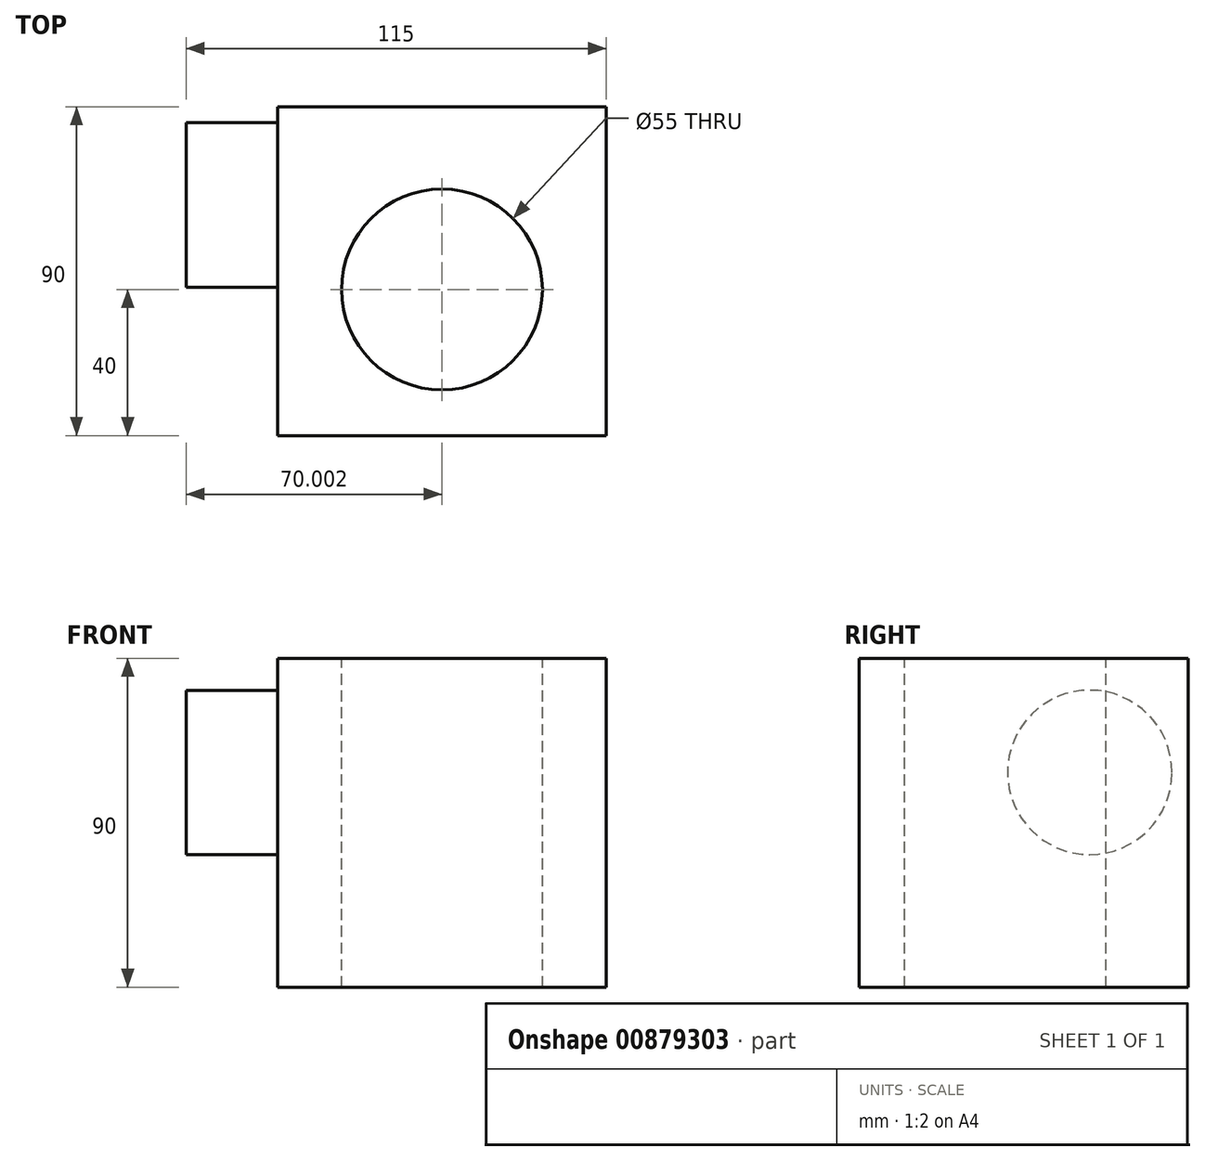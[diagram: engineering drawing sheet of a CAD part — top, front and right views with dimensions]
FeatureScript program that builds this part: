
annotation { "Feature Type Name" : "Feature", "Feature Type Description" : "" }
export const myFeature = defineFeature(function(context is Context, id is Id, definition is map)
    precondition{}
    {
        {
            var Q0;
            Q0=qCreatedBy(makeId("Front.planeOp"),FACE);
            var sketch = newSketch(context, id + "F0", { "sketchPlane" : qUnion([Q0])});
            skLineSegment(sketch, "E0.bottom", {"start": v(-42.19, 55.55) * mm, "end": v(47.81, 55.55) * mm});
            skLineSegment(sketch, "E0.top", {"start": v(-42.19, -34.45) * mm, "end": v(47.81, -34.45) * mm});
            skLineSegment(sketch, "E0.left", {"start": v(-42.19, 55.55) * mm, "end": v(-42.19, -34.45) * mm});
            skLineSegment(sketch, "E0.right", {"start": v(47.81, 55.55) * mm, "end": v(47.81, -34.45) * mm});
            skSolve(sketch);
        }
        {
            var Q0;
            Q0 = qSketchRegion(id + "F0", true);
            extrude(context, id + "F1", {"entities" : qUnion([Q0]), "depth" : 90 * mm, "offsetDistance" : 25 * mm});
        }
        {
            var Q0;
            Q0=makeQuery(id+"F1.opExtrude","SWEPT_FACE",FACE,{"disambiguationData":[OSD([sQuery(id+"F0.wireOp",EDGE,"E0.bottom")])]});
            var sketch = newSketch(context, id + "F2", { "sketchPlane" : qUnion([Q0])});
            skLineSegment(sketch, "E1", {"start": v(-42.19, 0) * mm, "end": v(47.81, -90) * mm, "construction": true});
            skLineSegment(sketch, "E2", {"start": v(47.81, 0) * mm, "end": v(-42.19, -90) * mm, "construction": true});
            skCircle(sketch, "E3", {"center": v(2.81, -50) * mm, "radius": 27.5 * mm});
            skSolve(sketch);
        }
        {
            var Q0;
            Q0 = qSketchRegion(id + "F2", true);
            extrude(context, id + "F3", {"entities" : qUnion([Q0]), "operationType" : NewBodyOperationType.REMOVE, "endBound" : BoundingType.UP_TO_NEXT, "oppositeDirection" : true, "depth" : 25 * mm, "offsetDistance" : 25 * mm});
        }
        {
            var Q0;
            Q0=makeQuery(id+"F1.opExtrude","SWEPT_FACE",FACE,{"disambiguationData":[OSD([sQuery(id+"F0.wireOp",EDGE,"E0.left")])]});
            var sketch = newSketch(context, id + "F4", { "sketchPlane" : qUnion([Q0])});
            skCircle(sketch, "E4", {"center": v(26.88, 24.34) * mm, "radius": 22.5 * mm});
            skSolve(sketch);
        }
        {
            var Q0;
            Q0 = qSketchRegion(id + "F4", true);
            extrude(context, id + "F5", {"entities" : qUnion([Q0]), "operationType" : NewBodyOperationType.ADD, "depth" : 25 * mm, "offsetDistance" : 25 * mm});
        }
    });
